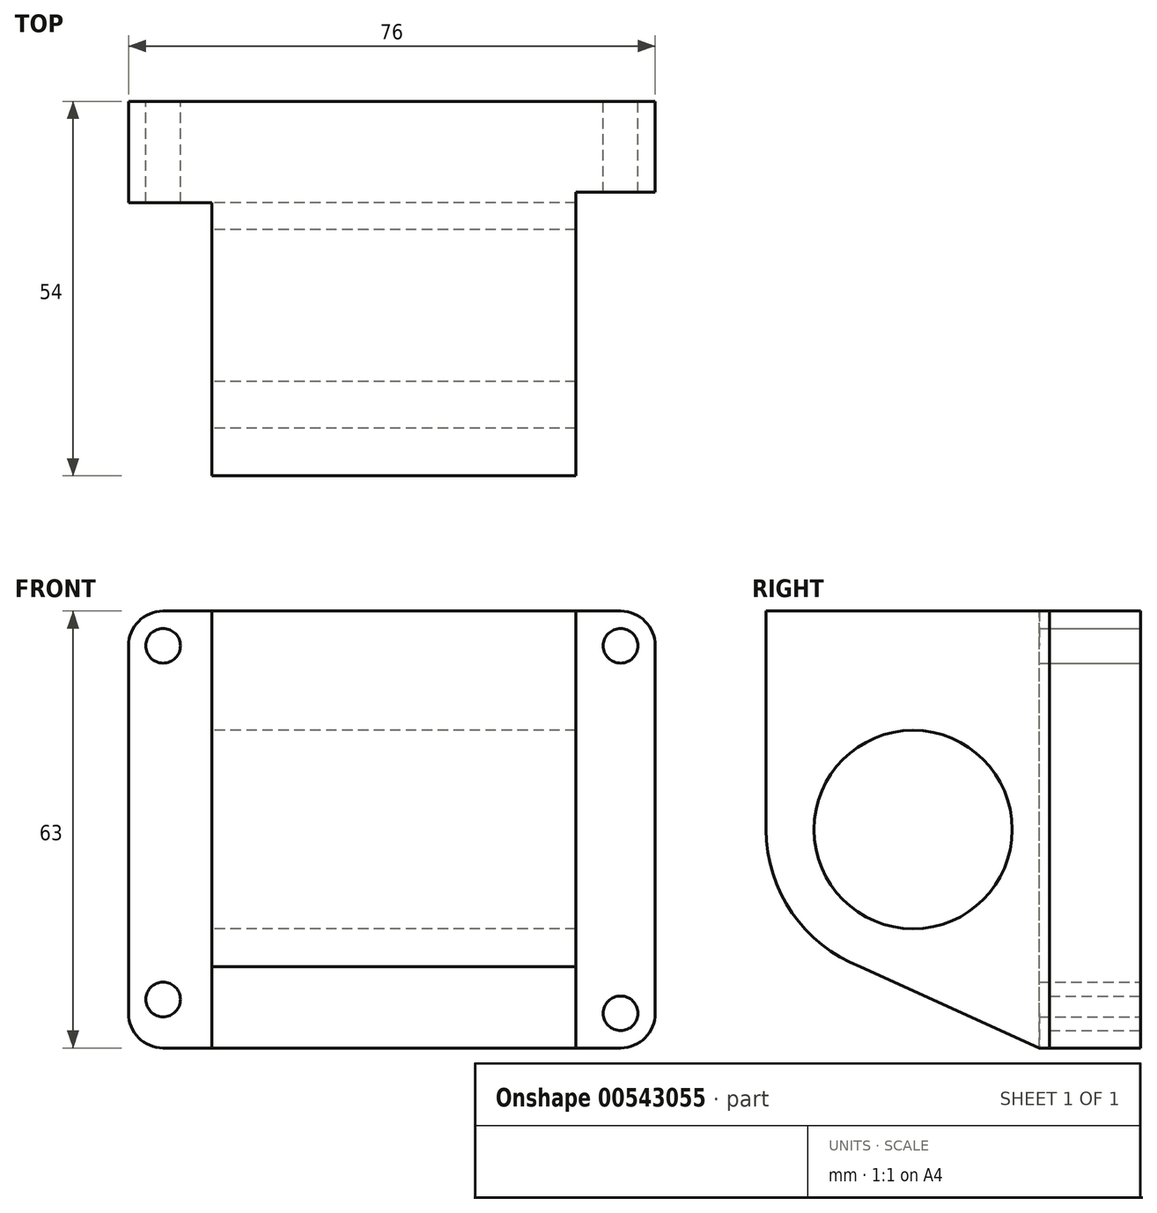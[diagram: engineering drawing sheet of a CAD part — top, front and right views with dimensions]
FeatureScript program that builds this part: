
annotation { "Feature Type Name" : "Feature", "Feature Type Description" : "" }
export const myFeature = defineFeature(function(context is Context, id is Id, definition is map)
    precondition{}
    {
        {
            var Q0;
            Q0=qCreatedBy(makeId("Front.planeOp"),FACE);
            var sketch = newSketch(context, id + "F0", { "sketchPlane" : qUnion([Q0])});
            skLineSegment(sketch, "E0.bottom", {"start": v(5, 0) * mm, "end": v(71, 0) * mm});
            skLineSegment(sketch, "E0.top", {"start": v(5, -63) * mm, "end": v(71, -63) * mm});
            skLineSegment(sketch, "E0.left", {"start": v(0, -5) * mm, "end": v(0, -58) * mm});
            skLineSegment(sketch, "E0.right", {"start": v(76, -5) * mm, "end": v(76, -58) * mm});
            skPoint(sketch, "E1.visualSharp", {"position": v(76, 0) * mm});
            skArc(sketch, "E1.filletArc", {"start": v(76, -5) * mm, "mid": v(74.54, -1.46) * mm, "end": v(71, 0) * mm});
            skPoint(sketch, "E2.visualSharp", {"position": v(76, -63) * mm});
            skArc(sketch, "E2.filletArc", {"start": v(71, -63) * mm, "mid": v(74.54, -61.54) * mm, "end": v(76, -58) * mm});
            skPoint(sketch, "E3.visualSharp", {"position": v(0, -63) * mm});
            skArc(sketch, "E3.filletArc", {"start": v(0, -58) * mm, "mid": v(1.46, -61.54) * mm, "end": v(5, -63) * mm});
            skPoint(sketch, "E4.visualSharp", {"position": v(0, 0) * mm});
            skArc(sketch, "E4.filletArc", {"start": v(5, 0) * mm, "mid": v(1.46, -1.46) * mm, "end": v(0, -5) * mm});
            skCircle(sketch, "E5", {"center": v(71, -5) * mm, "radius": 2.5 * mm});
            skCircle(sketch, "E6", {"center": v(71, -58) * mm, "radius": 2.5 * mm});
            skCircle(sketch, "E7", {"center": v(5, -5) * mm, "radius": 2.5 * mm});
            skCircle(sketch, "E8", {"center": v(5, -56) * mm, "radius": 2.5 * mm});
            skSolve(sketch);
        }
        {
            var Q0;
            Q0 = qSketchRegion(id + "F0", true);
            extrude(context, id + "F1", {"entities" : qUnion([Q0]), "depth" : 54 * mm, "offsetDistance" : 25 * mm});
        }
        {
            var Q0;
            Q0=qCreatedBy(makeId("Top.planeOp"),FACE);
            var sketch = newSketch(context, id + "F2", { "sketchPlane" : qUnion([Q0])});
            skLineSegment(sketch, "E9.bottom", {"start": v(0, -55) * mm, "end": v(12, -55) * mm});
            skLineSegment(sketch, "E9.top", {"start": v(0, -14.6) * mm, "end": v(12, -14.6) * mm});
            skLineSegment(sketch, "E9.left", {"start": v(0, -55) * mm, "end": v(0, -14.6) * mm});
            skLineSegment(sketch, "E9.right", {"start": v(12, -55) * mm, "end": v(12, -14.6) * mm});
            skLineSegment(sketch, "E10.bottom", {"start": v(76.52, -54.1) * mm, "end": v(64.52, -54.1) * mm});
            skLineSegment(sketch, "E10.top", {"start": v(76.52, -13.1) * mm, "end": v(64.52, -13.1) * mm});
            skLineSegment(sketch, "E10.left", {"start": v(76.52, -54.1) * mm, "end": v(76.52, -13.1) * mm});
            skLineSegment(sketch, "E10.right", {"start": v(64.52, -54.1) * mm, "end": v(64.52, -13.1) * mm});
            skSolve(sketch);
        }
        {
            var Q0;
            Q0 = qSketchRegion(id + "F2", true);
            extrude(context, id + "F3", {"entities" : qUnion([Q0]), "operationType" : NewBodyOperationType.REMOVE, "oppositeDirection" : true, "depth" : 65 * mm, "offsetDistance" : 25 * mm});
        }
        {
            var Q0;
            Q0=qCreatedBy(makeId("Right.planeOp"),FACE);
            var sketch = newSketch(context, id + "F4", { "sketchPlane" : qUnion([Q0])});
            skCircle(sketch, "E11", {"center": v(-32.8, -31.5) * mm, "radius": 14.3 * mm});
            skSolve(sketch);
        }
        {
            var Q0;
            Q0 = qSketchRegion(id + "F4", true);
            extrude(context, id + "F5", {"entities" : qUnion([Q0]), "operationType" : NewBodyOperationType.REMOVE, "depth" : 100 * mm, "offsetDistance" : 25 * mm});
        }
        {
            var Q0;
            Q0=makeQuery(id+"F3.boolean.opBoolean","COPY",FACE,{"derivedFrom":makeQuery(id+"F3.opExtrude","SWEPT_FACE",FACE,{"disambiguationData":[OSD([sQuery(id+"F2.wireOp",EDGE,"E9.right")])]})});
            var sketch = newSketch(context, id + "F6", { "sketchPlane" : qUnion([Q0])});
            skArc(sketch, "E12", {"start": v(40.41, -51.29) * mm, "mid": v(54, -31.23) * mm, "end": v(39.9, -11.53) * mm});
            skLineSegment(sketch, "E13", {"start": v(14.6, 0) * mm, "end": v(43.2, -13.03) * mm});
            skLineSegment(sketch, "E14", {"start": v(14.6, -63) * mm, "end": v(42.68, -50.26) * mm});
            skSolve(sketch);
        }
        {
            var Q0;
            {var subQ1=sQuery(id+"F2.wireOp",EDGE,"E9.right");var subQ2=makeQuery(id+"F3.opExtrude","SWEPT_FACE",FACE,{"disambiguationData":[OSD([subQ1])]});var subQ3=sQuery(id+"F0.wireOp",EDGE,"E0.top");var subQ4=makeQuery(id+"F3.boolean.opBoolean","INTERSECT",EDGE,{"derivedFrom":[makeQuery(id+"F1.opExtrude","SWEPT_FACE",FACE,{"disambiguationData":[OSD([subQ3])]}),subQ2]});Q0=makeQuery(id+"F6.imprint","IMPRINT",FACE,{"disambiguationData":[TD([[makeQuery(id+"F6.imprint","IMPRINT",EDGE,{"derivedFrom":subQ4}),-1.0]])]});}
            var Q1;
            {var subQ0=sQuery(id+"F2.wireOp",EDGE,"E9.right");var subQ1=makeQuery(id+"F3.boolean.opBoolean","COPY",EDGE,{"derivedFrom":makeQuery(id+"F3.opExtrude","CAP_EDGE",EDGE,{"disambiguationData":[OSD([subQ0])],"isStart":true})});Q1=makeQuery(id+"F6.imprint","IMPRINT",FACE,{"disambiguationData":[TD([[makeQuery(id+"F6.imprint","IMPRINT",EDGE,{"derivedFrom":subQ1}),1.0]])]});}
            extrude(context, id + "F7", {"entities" : qUnion([Q0, Q1]), "operationType" : NewBodyOperationType.REMOVE, "oppositeDirection" : true, "depth" : 100 * mm, "offsetDistance" : 25 * mm});
        }
    });
